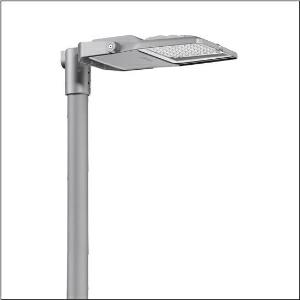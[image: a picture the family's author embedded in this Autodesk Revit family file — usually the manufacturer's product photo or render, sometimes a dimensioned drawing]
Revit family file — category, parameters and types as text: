
# Revit family: floodlight_fl_21_iq_mini___pl33t_5xa7771b4f3a_1cb2
name_source: partatom
category: Lighting Fixtures
units: mm (PartAtom-declared; Revit-internal decimal feet)

## family parameters
Cut with Voids When Loaded = No
Host = Face
Light Source = No
Part Type = Normal
Room Calculation Point = No
Round Connector Dimension = Use Diameter
Shared = No

## types (1)
- --- (1 x LED, 6420 lm, 45.5 W, 4000K)
    Apparent Load = 46 VA
    CIE Flux Codes = 26 75 99 100 100
    Color Rendering = 70
    Color Temperature = 4000K
    Default Elevation = 1800 mm
    Description = Floodlight FL 21 iQ mini, floodlight, primary light control with lens, of PMMA, primary optical cover: protective disc, of toughened safety glass, transparent, light distribution: PL33T, light emission: direct distribution, installation type: surface-mounted, LED, High Power LED, rated luminous flux: 6.420lm, luminous efficacy: 141lm/W, light colour: 740, colour temperature: 4000K, control: Auto-Match, Temp-Guard, Lumen-Switch, Night-Set, Smart-Wire, Light-Fading, Desk-Remote (wireless, voltage-free reading and setting of iQ features in the workshop via application-optimized NFC function/RFID function), optimised constant luminous flux control (CLO 2.0), with terminal, 6-pole, mains connection: 220..240V, AC, 50/60Hz, start of lifetime: 46W, end of service life: 48W, reduction: 22W, luminaire housing, of diecast aluminium, powder-coated, Siteco® metallic grey (DB 702S), corrosivity category C5 mid according to DIN EN ISO 12944, sealing non-destructively replaceable, please order mast flange separately, mast bracket, of steel, galvanised, powder-coated, Siteco® metallic grey (DB 702S), protection rating (complete): IP66, insulation class (complete): insulation class II (safety insulation), certification: CE, ENEC, VDE, protection symbol: D, impact resistance: IK08, permissible operating ambient temperature: -40..+40°C, permissible operating ambient temperature for outdoor applications: -40..+50°C, standard: DIN EN 12944, LABS conformity tested according to VDMA 24364:2018-05, packaging unit: 1 piece

Light Distribution: PL33T
    Height = 70 mm
    Lamp = 1 x LED
    Lamp Light Flux = 6420 lm
    Lamp Power = 45.5 W
    Lamp count = 1
    Length = 485 mm
    Luminous efficacy = 141 lm/W
    Manufacturer = Siteco
    ModVariant = No
    Model = 5XA7771B4F3A
    Number of Poles = 1
    OnlyDefault = Yes
    Power Factor = 1
    Product Name = Floodlight FL 21 iQ mini | PL33T
    Product group = floodlight | pylon annexe
    ProductGroupID = 6200
    Protection Class = Protection class II
    Protection Degree = IP 66
    RLX_Detail_Level = 1
    RLX_Emergency_Light_Flux = 0 lm
    RLX_Emergency_Type = 0
    RLX_Emergency_Type_DB = No
    RlxData = <blob elided: 101033 chars, md5=dc56ad26>
    Socket = socket
    Standby Power = 0 W
    System Light Flux = 6420 lm
    System Power = 46 W
    Type Comments = factory setting: luminous flux: 100 % | dim-lin: 254 | 463 mA
    Type Image = l_1007125.jpg
    URL = http://relux.com
    VarID = @adj_120509
    Voltage = 0 V
    Weight = 0.00 kg
    Width = 337 mm

## geometry (parser evidence)
native form markers: Blend x4, Sweep x12
no freeform markers — native parametric forms only
